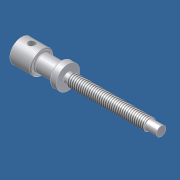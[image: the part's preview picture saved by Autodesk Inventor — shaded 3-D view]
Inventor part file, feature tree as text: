
AUTODESK INVENTOR PART (.ipt)
format: ipt  version: unknown  size: 225,792 bytes
history: native  units: in
note: dims shown in document units (in); Inventor stores cm internally (conversion verified against a paired STEP export)
features: sketch x2, revolve x1, thread x1, plane x1, hole x1, fillet x1
ambient origin geometry x8: Origin, YZ Plane, XZ Plane, XY Plane, X Axis, Y Axis, Z Axis, Center Point
bodies: Solid1 (feature_tree)
feature tree (7):
  revolve  "Revolution1"  [1 undecoded]
  thread  "Thread1"  [1 undecoded]
  plane  "Work Plane1"
  hole  "Hole1"  [1 undecoded]
  fillet  "Fillet1"  Radius=0.125in
  sketch  "Sketch1"  dims[d0=3.813in d1=0.3125in d2=0.219in]
  sketch  "Sketch2"  dims[d3=0.3125in d4=0.188in d5=0.125in d6=0.1562in d9=0.625in d10=2.5in d11=90.0deg d12=2.063in d13=0.0in d14=0.28in d15=0.185in d16=0.75in d17=0.375in d18=0.25in d19=0.5635in d20=1.0in d21=0.0in d22=0.0313in d23=0.125in d24=0.0312in d25=2.188in d26=0.313in]
note: 3 required parameter values undecoded (feature->parameter linkage not recoverable at this tier; creation-order binding heuristic only, values carry confidence <= 0.55)